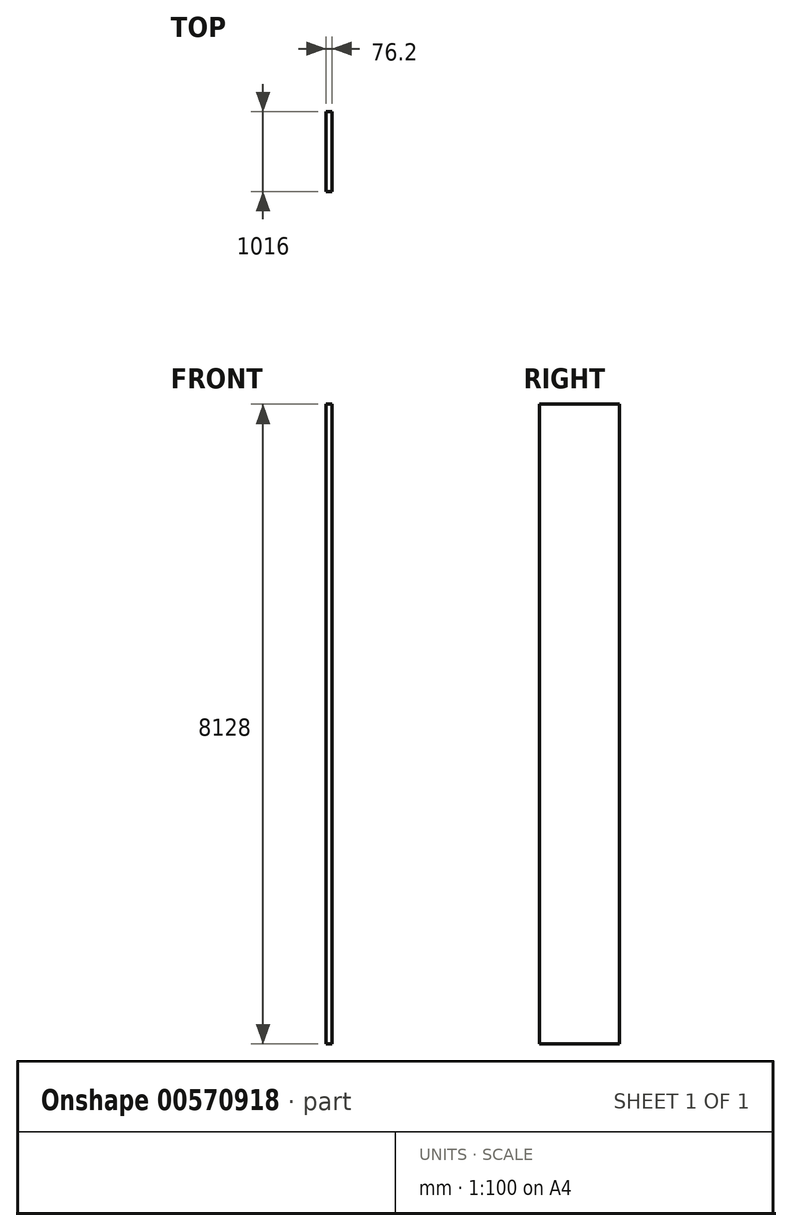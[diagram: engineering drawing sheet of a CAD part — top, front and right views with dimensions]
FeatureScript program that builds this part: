
annotation { "Feature Type Name" : "Feature", "Feature Type Description" : "" }
export const myFeature = defineFeature(function(context is Context, id is Id, definition is map)
    precondition{}
    {
        {
            var Q0;
            Q0=qCreatedBy(makeId("Top.planeOp"),FACE);
            var sketch = newSketch(context, id + "F0", { "sketchPlane" : qUnion([Q0])});
            skLineSegment(sketch, "E0", {"start": v(0, 0) * mm, "end": v(0, 1016) * mm});
            skLineSegment(sketch, "E1", {"start": v(0, 1016) * mm, "end": v(76.2, 1016) * mm});
            skLineSegment(sketch, "E2", {"start": v(76.2, 1016) * mm, "end": v(76.2, 0) * mm});
            skLineSegment(sketch, "E3", {"start": v(76.2, 0) * mm, "end": v(0, 0) * mm});
            skSolve(sketch);
        }
        {
            var Q0;
            Q0=makeQuery(id+"F0.imprint","IMPRINT",FACE,{"disambiguationData":[TD([[makeQuery(id+"F0.imprint","IMPRINT",EDGE,{"derivedFrom":sQuery(id+"F0.wireOp",EDGE,"E0")}),-1.0]])]});
            extrude(context, id + "F1", {"entities" : qUnion([Q0]), "depth" : 8128 * mm, "offsetDistance" : 25.4 * mm});
        }
    });
